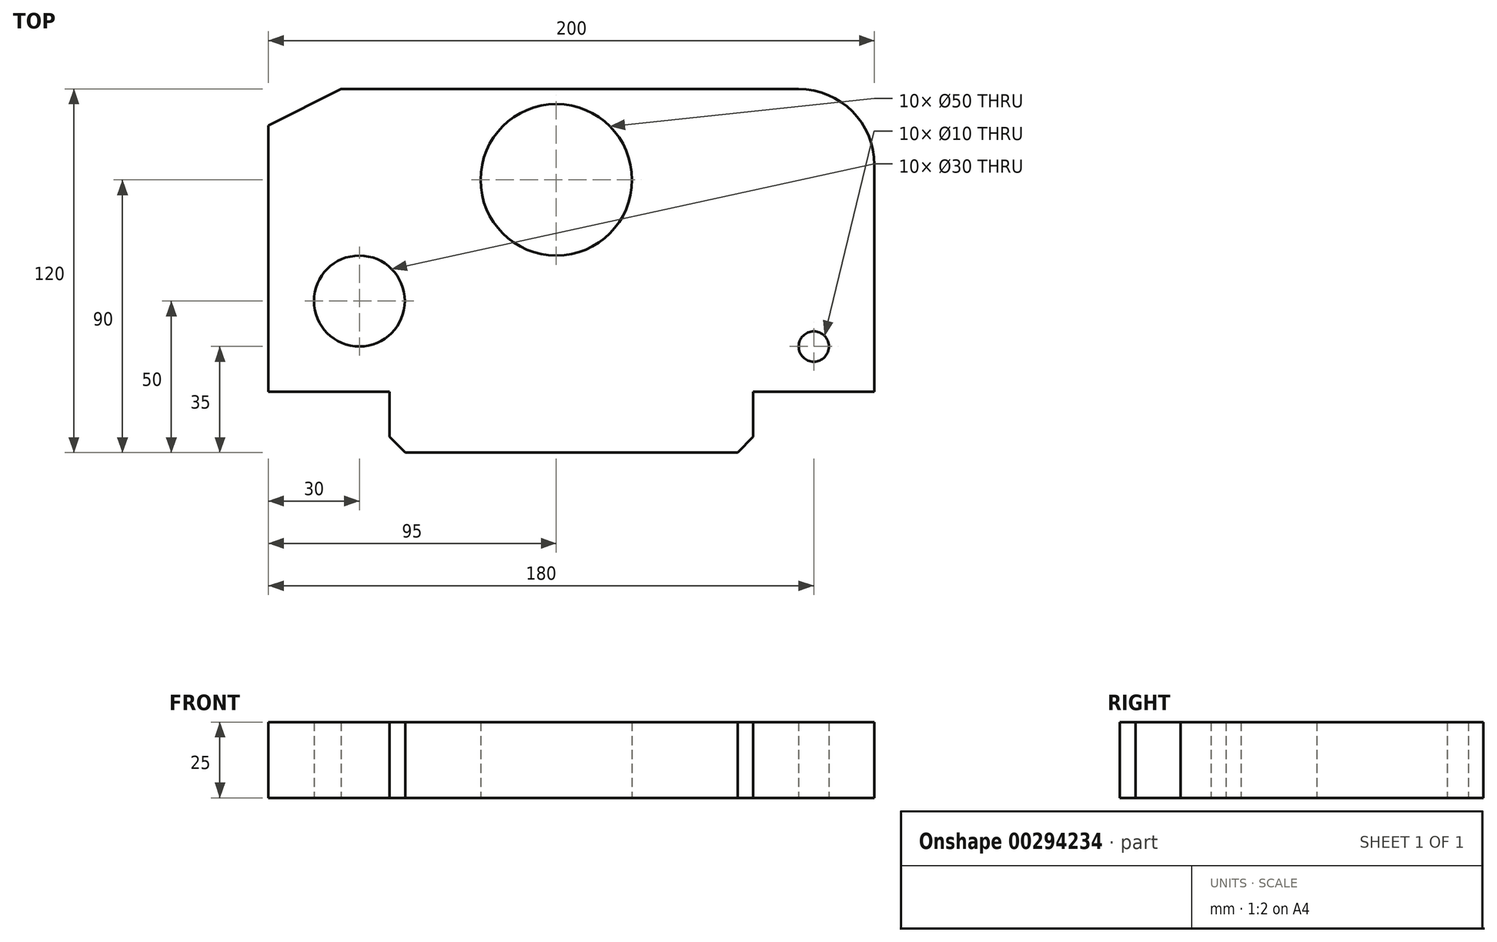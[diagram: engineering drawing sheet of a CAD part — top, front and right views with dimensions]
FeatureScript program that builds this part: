
annotation { "Feature Type Name" : "Feature", "Feature Type Description" : "" }
export const myFeature = defineFeature(function(context is Context, id is Id, definition is map)
    precondition{}
    {
        {
            var Q0;
            Q0=qCreatedBy(makeId("Top.planeOp"),FACE);
            var sketch = newSketch(context, id + "F0", { "sketchPlane" : qUnion([Q0])});
            skLineSegment(sketch, "E0", {"start": v(0, 0) * mm, "end": v(54.82, 0) * mm});
            skLineSegment(sketch, "E1", {"start": v(0, 0) * mm, "end": v(-54.82, 0) * mm});
            skLineSegment(sketch, "E2", {"start": v(-60, 5.18) * mm, "end": v(-60, 20) * mm});
            skLineSegment(sketch, "E3", {"start": v(-60, 20) * mm, "end": v(-70, 20) * mm});
            skLineSegment(sketch, "E4", {"start": v(-100, 20) * mm, "end": v(-100, 108) * mm});
            skLineSegment(sketch, "E5", {"start": v(-76, 120) * mm, "end": v(75, 120) * mm});
            skLineSegment(sketch, "E6", {"start": v(100, 95) * mm, "end": v(100, 35) * mm});
            skLineSegment(sketch, "E7", {"start": v(60, 5.18) * mm, "end": v(60, 20) * mm});
            skLineSegment(sketch, "E8", {"start": v(60, 20) * mm, "end": v(100, 20) * mm});
            skLineSegment(sketch, "E9", {"start": v(54.82, 0) * mm, "end": v(60, 5.18) * mm});
            skLineSegment(sketch, "E10", {"start": v(-60, 5.18) * mm, "end": v(-54.82, 0) * mm});
            skLineSegment(sketch, "E11", {"start": v(-76, 120) * mm, "end": v(-100, 108) * mm});
            skPoint(sketch, "E12.end.orphan", {"position": v(60, 0) * mm});
            skPoint(sketch, "E13.visualSharp", {"position": v(100, 120) * mm});
            skArc(sketch, "E13.filletArc", {"start": v(100, 95) * mm, "mid": v(92.68, 112.68) * mm, "end": v(75, 120) * mm});
            skLineSegment(sketch, "E14", {"start": v(-76, 120) * mm, "end": v(-5, 120) * mm});
            skCircle(sketch, "E15", {"center": v(-5, 90) * mm, "radius": 25 * mm});
            skCircle(sketch, "E16", {"center": v(80, 35) * mm, "radius": 5 * mm});
            skLineSegment(sketch, "E17", {"start": v(100, 35) * mm, "end": v(100, 20) * mm});
            skCircle(sketch, "E18", {"center": v(-70, 50) * mm, "radius": 15 * mm});
            skLineSegment(sketch, "E19", {"start": v(-70, 20) * mm, "end": v(-100, 20) * mm});
            skSolve(sketch);
        }
        {
            var Q0;
            Q0=makeQuery(id+"F0.imprint","IMPRINT",FACE,{"disambiguationData":[TD([[makeQuery(id+"F0.imprint","IMPRINT",EDGE,{"derivedFrom":sQuery(id+"F0.wireOp",EDGE,"E0")}),1.0]])]});
            extrude(context, id + "F1", {"entities" : qUnion([Q0]), "depth" : 25 * mm});
        }
    });
